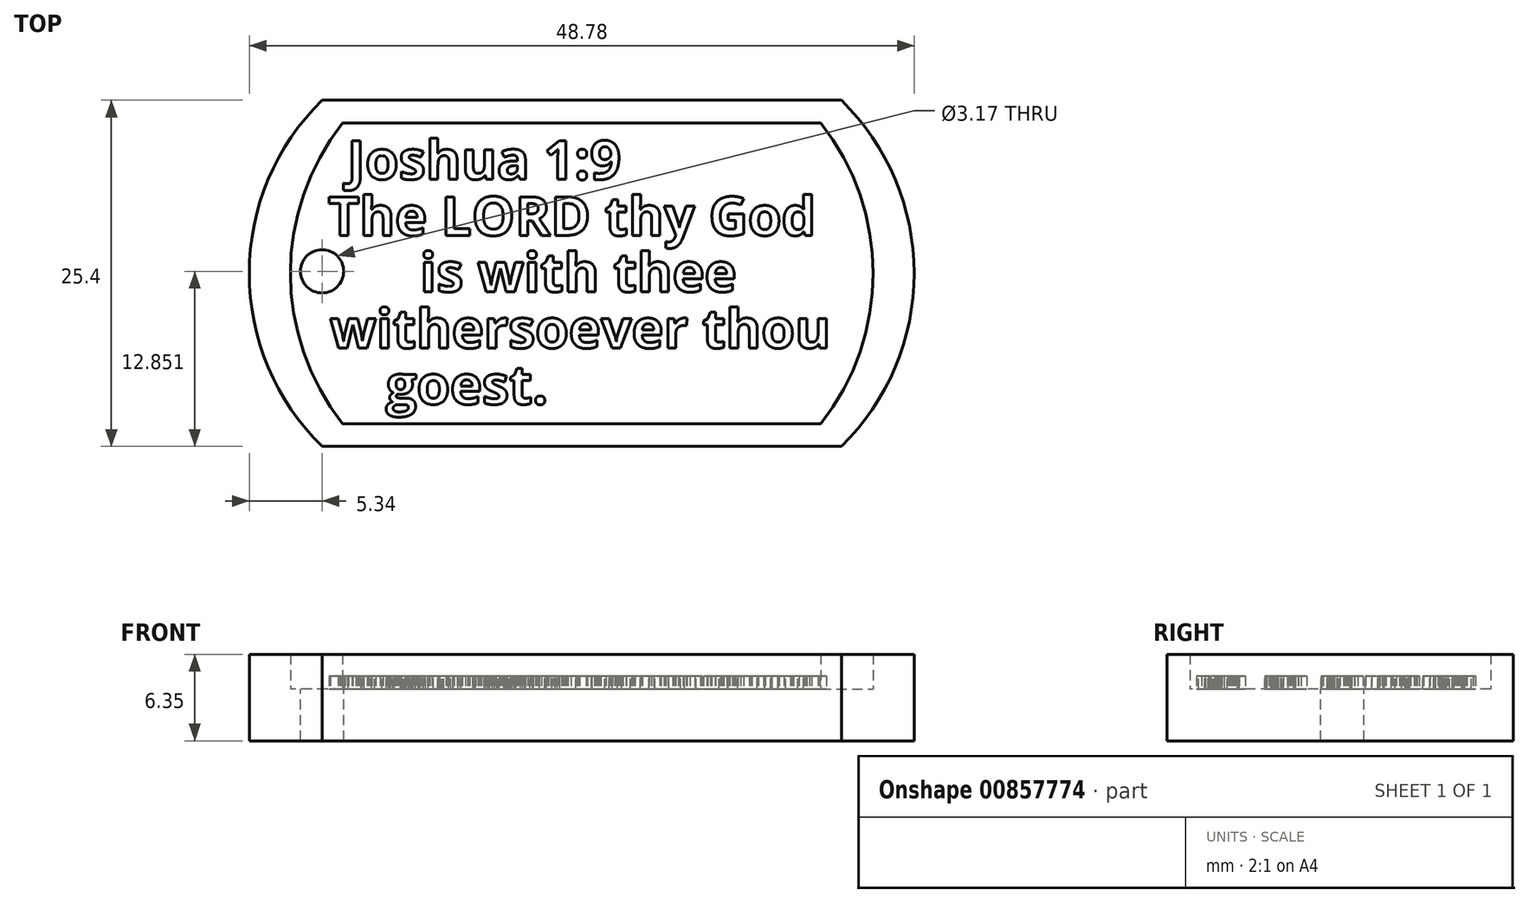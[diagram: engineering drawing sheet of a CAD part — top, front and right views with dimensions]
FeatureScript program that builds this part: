
annotation { "Feature Type Name" : "Feature", "Feature Type Description" : "" }
export const myFeature = defineFeature(function(context is Context, id is Id, definition is map)
    precondition{}
    {
        {
            var Q0;
            Q0=qCreatedBy(makeId("Top.planeOp"),FACE);
            var sketch = newSketch(context, id + "F0", { "sketchPlane" : qUnion([Q0])});
            skLineSegment(sketch, "E0.bottom", {"start": v(19.05, -12.7) * mm, "end": v(-19.05, -12.7) * mm});
            skLineSegment(sketch, "E0.top", {"start": v(19.05, 12.7) * mm, "end": v(-19.05, 12.7) * mm});
            skPoint(sketch, "E0.middle", {"position": v(0, 0) * mm});
            skArc(sketch, "E1", {"start": v(19.05, -12.7) * mm, "mid": v(24.39, 0) * mm, "end": v(19.05, 12.7) * mm});
            skArc(sketch, "E2", {"start": v(-19.05, 12.7) * mm, "mid": v(-24.39, 0) * mm, "end": v(-19.05, -12.7) * mm});
            skLineSegment(sketch, "E3.bottom", {"start": v(17.54, -11.03) * mm, "end": v(-17.54, -11.03) * mm});
            skLineSegment(sketch, "E3.top", {"start": v(17.54, 11.03) * mm, "end": v(-17.54, 11.03) * mm});
            skLineSegment(sketch, "E4", {"start": v(-19.05, 12.7) * mm, "end": v(19.05, 12.7) * mm});
            skLineSegment(sketch, "E5", {"start": v(-19.05, -12.7) * mm, "end": v(19.05, -12.7) * mm});
            skArc(sketch, "E6", {"start": v(-17.54, 11.03) * mm, "mid": v(-21.37, 0) * mm, "end": v(-17.54, -11.03) * mm});
            skArc(sketch, "E7", {"start": v(17.54, -11.03) * mm, "mid": v(21.37, 0) * mm, "end": v(17.54, 11.03) * mm});
            skSolve(sketch);
        }
        {
            var Q0;
            Q0=makeQuery(id+"F0.imprint","IMPRINT",FACE,{"disambiguationData":[TD([[makeQuery(id+"F0.imprint","IMPRINT",EDGE,{"derivedFrom":sQuery(id+"F0.wireOp",EDGE,"E1")}),1.0]])]});
            extrude(context, id + "F1", {"entities" : qUnion([Q0]), "depth" : 6.35 * mm, "offsetDistance" : 25.4 * mm});
        }
        {
            var Q0;
            Q0=makeQuery(id+"F0.imprint","IMPRINT",FACE,{"disambiguationData":[TD([[makeQuery(id+"F0.imprint","IMPRINT",EDGE,{"derivedFrom":sQuery(id+"F0.wireOp",EDGE,"E3.bottom")}),-1.0]])]});
            extrude(context, id + "F2", {"entities" : qUnion([Q0]), "operationType" : NewBodyOperationType.ADD, "depth" : 3.8 * mm, "offsetDistance" : 25.4 * mm});
        }
        {
            var Q0;
            Q0=makeQuery(id+"F2.opExtrude","CAP_FACE",FACE,{"disambiguationData":[OSD([sQuery(id+"F0.wireOp",EDGE,"E3.bottom"),sQuery(id+"F0.wireOp",EDGE,"E3.top"),sQuery(id+"F0.wireOp",EDGE,"E6"),sQuery(id+"F0.wireOp",EDGE,"E7")])],"isStart":false});
            var sketch = newSketch(context, id + "F3", { "sketchPlane" : qUnion([Q0])});
            skText(sketch, "E8", { "text": "Joshua 1:9", "fontName": "OpenSans-Bold.ttf"});
            skPoint(sketch, "E9", {"position": v(18, 11.65) * mm});
            skText(sketch, "E10", { "text": "is with thee", "fontName": "OpenSans-Bold.ttf"});
            skText(sketch, "E11", { "text": "The LORD thy God", "fontName": "OpenSans-Bold.ttf"});
            skText(sketch, "E12", { "text": "withersoever thou ", "fontName": "OpenSans-Bold.ttf"});
            skText(sketch, "E13", { "text": "goest.", "fontName": "OpenSans-Bold.ttf"});
            const initialGuessF3  = {"E8": [-0.0172, 0.0069, 1, 0, 0.00286], "E10": [-0.01187, -0.00135, 1, 0, 0.00286], "E11": [-0.0186, 0.00278, 1, 0, 0.00286], "E12": [-0.01848, -0.00548, 1, 0, 0.00286], "E13": [-0.01436, -0.0096, 1, 0, 0.00286]};
            skSetInitialGuess(sketch, initialGuessF3);
            skSolve(sketch);
        }
        {
            var Q0;
            Q0 = qSketchRegion(id + "F3", true);
            extrude(context, id + "F4", {"entities" : qUnion([Q0]), "operationType" : NewBodyOperationType.ADD, "depth" : 0.95 * mm, "offsetDistance" : 25.4 * mm});
        }
        {
            var Q0;
            {var subQ0=sQuery(id+"F0.wireOp",EDGE,"E3.bottom");var subQ1=sQuery(id+"F0.wireOp",EDGE,"E6");var subQ2=sQuery(id+"F0.wireOp",EDGE,"E7");var subQ3=sQuery(id+"F0.wireOp",EDGE,"E3.top");Q0=makeQuery(id+"F4.boolean.opBoolean","SPLIT",FACE,{"disambiguationData":[TD([makeQuery(id+"F1.opExtrude","SWEPT_FACE",FACE,{"disambiguationData":[OSD([subQ0])]})])],"derivedFrom":makeQuery(id+"F2.opExtrude","CAP_FACE",FACE,{"disambiguationData":[OSD([subQ0,subQ3,subQ1,subQ2])],"isStart":false})});}
            var sketch = newSketch(context, id + "F5", { "sketchPlane" : qUnion([Q0])});
            skCircle(sketch, "E14", {"center": v(-19.05, 0.15) * mm, "radius": 1.59 * mm});
            skSolve(sketch);
        }
        {
            var Q0;
            Q0 = qSketchRegion(id + "F5", true);
            extrude(context, id + "F6", {"entities" : qUnion([Q0]), "operationType" : NewBodyOperationType.REMOVE, "oppositeDirection" : true, "depth" : 25.4 * mm, "offsetDistance" : 25.4 * mm});
        }
    });
